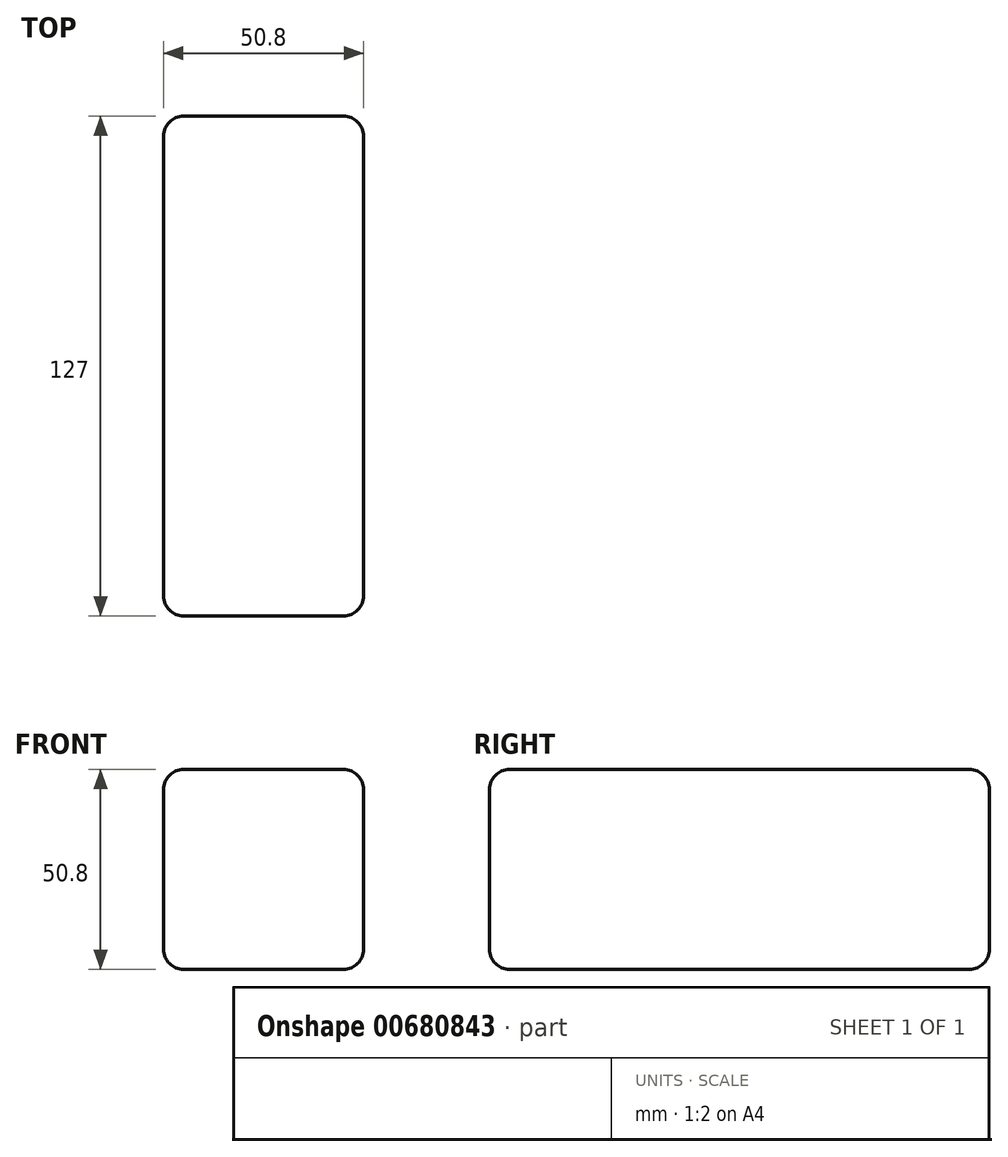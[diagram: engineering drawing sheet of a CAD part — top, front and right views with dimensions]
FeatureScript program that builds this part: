
annotation { "Feature Type Name" : "Feature", "Feature Type Description" : "" }
export const myFeature = defineFeature(function(context is Context, id is Id, definition is map)
    precondition{}
    {
        {
            var Q0;
            Q0=qCreatedBy(makeId("Front.planeOp"),FACE);
            var sketch = newSketch(context, id + "F0", { "sketchPlane" : qUnion([Q0])});
            skLineSegment(sketch, "E0.bottom", {"start": v(0, 0) * mm, "end": v(50.8, 0) * mm});
            skLineSegment(sketch, "E0.top", {"start": v(0, 50.8) * mm, "end": v(50.8, 50.8) * mm});
            skLineSegment(sketch, "E0.left", {"start": v(0, 0) * mm, "end": v(0, 50.8) * mm});
            skLineSegment(sketch, "E0.right", {"start": v(50.8, 0) * mm, "end": v(50.8, 50.8) * mm});
            skSolve(sketch);
        }
        {
            var Q0;
            Q0=makeQuery(id+"F0.imprint","IMPRINT",FACE,{"disambiguationData":[TD([[makeQuery(id+"F0.imprint","IMPRINT",EDGE,{"derivedFrom":sQuery(id+"F0.wireOp",EDGE,"E0.bottom")}),1.0]])]});
            extrude(context, id + "F1", {"entities" : qUnion([Q0]), "depth" : 127 * mm, "offsetDistance" : 25.4 * mm});
        }
        {
            var Q0;
            Q0=makeQuery(id+"F1.opExtrude","SWEPT_EDGE",EDGE,{"disambiguationData":[OSD([sQuery(id+"F0.wireOp",EDGE,"E0.top"),sQuery(id+"F0.wireOp",EDGE,"E0.left")])]});
            var Q1;
            Q1=makeQuery(id+"F1.opExtrude","SWEPT_EDGE",EDGE,{"disambiguationData":[OSD([sQuery(id+"F0.wireOp",EDGE,"E0.top"),sQuery(id+"F0.wireOp",EDGE,"E0.right")])]});
            var Q2;
            Q2=makeQuery(id+"F1.opExtrude","CAP_EDGE",EDGE,{"disambiguationData":[OSD([sQuery(id+"F0.wireOp",EDGE,"E0.top")])],"isStart":true});
            var Q3;
            Q3=makeQuery(id+"F1.opExtrude","CAP_EDGE",EDGE,{"disambiguationData":[OSD([sQuery(id+"F0.wireOp",EDGE,"E0.right")])],"isStart":true});
            var Q4;
            Q4=makeQuery(id+"F1.opExtrude","CAP_EDGE",EDGE,{"disambiguationData":[OSD([sQuery(id+"F0.wireOp",EDGE,"E0.bottom")])],"isStart":true});
            var Q5;
            Q5=makeQuery(id+"F1.opExtrude","CAP_FACE",FACE,{"disambiguationData":[OSD([sQuery(id+"F0.wireOp",EDGE,"E0.bottom"),sQuery(id+"F0.wireOp",EDGE,"E0.top"),sQuery(id+"F0.wireOp",EDGE,"E0.left"),sQuery(id+"F0.wireOp",EDGE,"E0.right")])],"isStart":true});
            var Q6;
            Q6=makeQuery(id+"F1.opExtrude","SWEPT_EDGE",EDGE,{"disambiguationData":[OSD([sQuery(id+"F0.wireOp",EDGE,"E0.bottom"),sQuery(id+"F0.wireOp",EDGE,"E0.right")])]});
            var Q7;
            Q7=makeQuery(id+"F1.opExtrude","SWEPT_EDGE",EDGE,{"disambiguationData":[OSD([sQuery(id+"F0.wireOp",EDGE,"E0.bottom"),sQuery(id+"F0.wireOp",EDGE,"E0.left")])]});
            var Q8;
            Q8=makeQuery(id+"F1.opExtrude","CAP_EDGE",EDGE,{"disambiguationData":[OSD([sQuery(id+"F0.wireOp",EDGE,"E0.bottom")])],"isStart":false});
            var Q9;
            Q9=makeQuery(id+"F1.opExtrude","CAP_EDGE",EDGE,{"disambiguationData":[OSD([sQuery(id+"F0.wireOp",EDGE,"E0.left")])],"isStart":false});
            var Q10;
            Q10=makeQuery(id+"F1.opExtrude","CAP_EDGE",EDGE,{"disambiguationData":[OSD([sQuery(id+"F0.wireOp",EDGE,"E0.top")])],"isStart":false});
            var Q11;
            Q11=makeQuery(id+"F1.opExtrude","CAP_EDGE",EDGE,{"disambiguationData":[OSD([sQuery(id+"F0.wireOp",EDGE,"E0.right")])],"isStart":false});
            fillet(context, id + "F2", {"entities" : qUnion([Q0, Q1, Q2, Q3, Q4, Q5, Q6, Q7, Q8, Q9, Q10, Q11]), "radius" : 5.08 * mm, "tangentPropagation" : true, "allowEdgeOverflow" : false});
        }
    });
